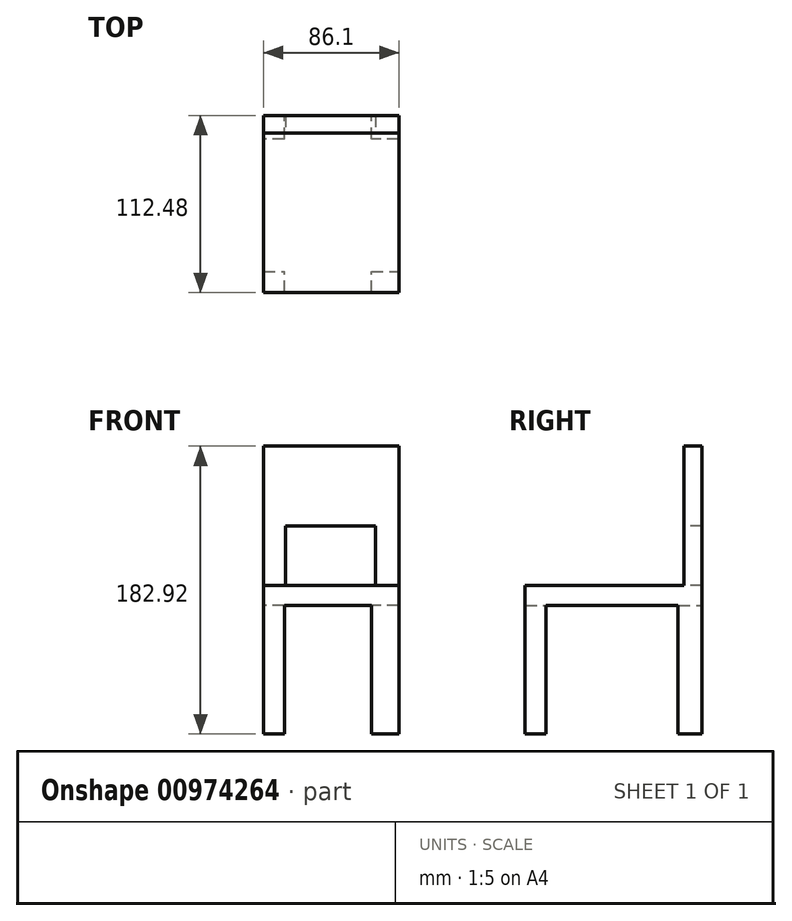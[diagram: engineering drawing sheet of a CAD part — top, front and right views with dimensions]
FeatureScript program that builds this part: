
annotation { "Feature Type Name" : "Feature", "Feature Type Description" : "" }
export const myFeature = defineFeature(function(context is Context, id is Id, definition is map)
    precondition{}
    {
        {
            var Q0;
            Q0=qCreatedBy(makeId("Top.planeOp"),FACE);
            var sketch = newSketch(context, id + "F0", { "sketchPlane" : qUnion([Q0])});
            skLineSegment(sketch, "E0.bottom", {"start": v(-38.64, 51.36) * mm, "end": v(47.46, 51.36) * mm});
            skLineSegment(sketch, "E0.top", {"start": v(-38.64, -61.12) * mm, "end": v(47.46, -61.12) * mm});
            skLineSegment(sketch, "E0.left", {"start": v(-38.64, 51.36) * mm, "end": v(-38.64, -61.12) * mm});
            skLineSegment(sketch, "E0.right", {"start": v(47.46, 51.36) * mm, "end": v(47.46, -61.12) * mm});
            skSolve(sketch);
        }
        {
            var Q0;
            Q0=makeQuery(id+"F0.imprint","IMPRINT",FACE,{"disambiguationData":[TD([[makeQuery(id+"F0.imprint","IMPRINT",EDGE,{"derivedFrom":sQuery(id+"F0.wireOp",EDGE,"E0.bottom")}),-1.0]])]});
            extrude(context, id + "F1", {"entities" : qUnion([Q0]), "depth" : 12.7 * mm, "offsetDistance" : 25.4 * mm});
        }
        {
            var Q0;
            Q0=makeQuery(id+"F1.opExtrude","CAP_FACE",FACE,{"disambiguationData":[OSD([sQuery(id+"F0.wireOp",EDGE,"E0.bottom"),sQuery(id+"F0.wireOp",EDGE,"E0.top"),sQuery(id+"F0.wireOp",EDGE,"E0.left"),sQuery(id+"F0.wireOp",EDGE,"E0.right")])],"isStart":false});
            var sketch = newSketch(context, id + "F2", { "sketchPlane" : qUnion([Q0])});
            skLineSegment(sketch, "E1", {"start": v(32.6, 51.36) * mm, "end": v(32.6, -61.12) * mm});
            skLineSegment(sketch, "E2", {"start": v(-24.73, 51.36) * mm, "end": v(-24.73, -61.12) * mm});
            skLineSegment(sketch, "E3", {"start": v(47.46, 40.03) * mm, "end": v(-38.64, 40.03) * mm});
            skLineSegment(sketch, "E4", {"start": v(47.46, -45.23) * mm, "end": v(-38.64, -45.23) * mm});
            skSolve(sketch);
        }
        {
            var Q0;
            {var subQ0=sQuery(id+"F2.wireOp",EDGE,"E2");var subQ1=makeQuery(id+"F1.opExtrude","CAP_EDGE",EDGE,{"disambiguationData":[OSD([sQuery(id+"F0.wireOp",EDGE,"E0.bottom")])],"isStart":false});var subQ2=makeQuery(id+"F2.imprint","INTERSECT",VERTEX,{"derivedFrom":[subQ1,subQ0]});Q0=makeQuery(id+"F2.imprint","IMPRINT",FACE,{"disambiguationData":[TD([[makeQuery(id+"F2.imprint","IMPRINT",EDGE,{"disambiguationData":[TD([[subQ2,-1.0]])],"derivedFrom":subQ0}),-1.0]])]});}
            var Q1;
            {var subQ0=sQuery(id+"F2.wireOp",EDGE,"E1");var subQ1=makeQuery(id+"F1.opExtrude","CAP_EDGE",EDGE,{"disambiguationData":[OSD([sQuery(id+"F0.wireOp",EDGE,"E0.bottom")])],"isStart":false});var subQ2=makeQuery(id+"F2.imprint","INTERSECT",VERTEX,{"derivedFrom":[subQ1,subQ0]});Q1=makeQuery(id+"F2.imprint","IMPRINT",FACE,{"disambiguationData":[TD([[makeQuery(id+"F2.imprint","IMPRINT",EDGE,{"disambiguationData":[TD([[subQ2,-1.0]])],"derivedFrom":subQ0}),1.0]])]});}
            extrude(context, id + "F3", {"entities" : qUnion([Q0, Q1]), "operationType" : NewBodyOperationType.ADD, "depth" : 88.57 * mm, "offsetDistance" : 25.4 * mm});
        }
        {
            var Q0;
            Q0=makeQuery(id+"F1.opExtrude","CAP_FACE",FACE,{"disambiguationData":[OSD([sQuery(id+"F0.wireOp",EDGE,"E0.bottom"),sQuery(id+"F0.wireOp",EDGE,"E0.top"),sQuery(id+"F0.wireOp",EDGE,"E0.left"),sQuery(id+"F0.wireOp",EDGE,"E0.right")])],"isStart":true});
            var sketch = newSketch(context, id + "F4", { "sketchPlane" : qUnion([Q0])});
            skLineSegment(sketch, "E5", {"start": v(-38.64, 47.8) * mm, "end": v(47.46, 47.8) * mm});
            skLineSegment(sketch, "E6", {"start": v(47.46, -36.21) * mm, "end": v(-38.64, -36.21) * mm});
            skLineSegment(sketch, "E7", {"start": v(29.9, 61.12) * mm, "end": v(29.9, -51.36) * mm});
            skLineSegment(sketch, "E8", {"start": v(-25.25, 61.12) * mm, "end": v(-25.25, -51.36) * mm});
            skSolve(sketch);
        }
        {
            var Q0;
            {var subQ0=sQuery(id+"F4.wireOp",EDGE,"E5");var subQ1=makeQuery(id+"F1.opExtrude","CAP_EDGE",EDGE,{"disambiguationData":[OSD([sQuery(id+"F0.wireOp",EDGE,"E0.right")])],"isStart":true});var subQ2=makeQuery(id+"F4.imprint","INTERSECT",VERTEX,{"derivedFrom":[subQ1,subQ0]});Q0=makeQuery(id+"F4.imprint","IMPRINT",FACE,{"disambiguationData":[TD([[makeQuery(id+"F4.imprint","IMPRINT",EDGE,{"disambiguationData":[TD([[subQ2,1.0]])],"derivedFrom":subQ0}),1.0]])]});}
            var Q1;
            {var subQ0=sQuery(id+"F4.wireOp",EDGE,"E6");var subQ1=makeQuery(id+"F1.opExtrude","CAP_EDGE",EDGE,{"disambiguationData":[OSD([sQuery(id+"F0.wireOp",EDGE,"E0.right")])],"isStart":true});var subQ2=makeQuery(id+"F4.imprint","INTERSECT",VERTEX,{"derivedFrom":[subQ1,subQ0]});Q1=makeQuery(id+"F4.imprint","IMPRINT",FACE,{"disambiguationData":[TD([[makeQuery(id+"F4.imprint","IMPRINT",EDGE,{"disambiguationData":[TD([[subQ2,-1.0]])],"derivedFrom":subQ0}),1.0]])]});}
            var Q2;
            {var subQ0=sQuery(id+"F4.wireOp",EDGE,"E6");var subQ1=makeQuery(id+"F1.opExtrude","CAP_EDGE",EDGE,{"disambiguationData":[OSD([sQuery(id+"F0.wireOp",EDGE,"E0.left")])],"isStart":true});var subQ2=makeQuery(id+"F4.imprint","INTERSECT",VERTEX,{"derivedFrom":[subQ1,subQ0]});Q2=makeQuery(id+"F4.imprint","IMPRINT",FACE,{"disambiguationData":[TD([[makeQuery(id+"F4.imprint","IMPRINT",EDGE,{"disambiguationData":[TD([[subQ2,1.0]])],"derivedFrom":subQ0}),1.0]])]});}
            var Q3;
            {var subQ0=sQuery(id+"F4.wireOp",EDGE,"E5");var subQ1=makeQuery(id+"F1.opExtrude","CAP_EDGE",EDGE,{"disambiguationData":[OSD([sQuery(id+"F0.wireOp",EDGE,"E0.left")])],"isStart":true});var subQ2=makeQuery(id+"F4.imprint","INTERSECT",VERTEX,{"derivedFrom":[subQ1,subQ0]});Q3=makeQuery(id+"F4.imprint","IMPRINT",FACE,{"disambiguationData":[TD([[makeQuery(id+"F4.imprint","IMPRINT",EDGE,{"disambiguationData":[TD([[subQ2,-1.0]])],"derivedFrom":subQ0}),1.0]])]});}
            extrude(context, id + "F5", {"entities" : qUnion([Q0, Q1, Q2, Q3]), "operationType" : NewBodyOperationType.ADD, "depth" : 71.5 * mm, "offsetDistance" : 25.4 * mm});
        }
        {
            var Q0;
            Q0=makeQuery(id+"F3.opExtrude","SWEPT_FACE",FACE,{"disambiguationData":[OSD([sQuery(id+"F2.wireOp",EDGE,"E2")])]});
            var sketch = newSketch(context, id + "F6", { "sketchPlane" : qUnion([Q0])});
            skLineSegment(sketch, "E9", {"start": v(51.36, 50.62) * mm, "end": v(40.03, 50.62) * mm});
            skPoint(sketch, "E9.endSnap0", {"position": v(40.03, 56.98) * mm});
            skSolve(sketch);
        }
        {
            var Q0;
            {var subQ0=sQuery(id+"F6.wireOp",EDGE,"E9");Q0=makeQuery(id+"F6.imprint","IMPRINT",FACE,{"disambiguationData":[TD([[makeQuery(id+"F6.imprint","IMPRINT",EDGE,{"derivedFrom":subQ0}),-1.0]])]});}
            var Q1;
            Q1=makeQuery(id+"F3.opExtrude","SWEPT_FACE",FACE,{"disambiguationData":[OSD([sQuery(id+"F2.wireOp",EDGE,"E1")])]});
            extrude(context, id + "F7", {"entities" : qUnion([Q0]), "operationType" : NewBodyOperationType.ADD, "endBound" : BoundingType.UP_TO_SURFACE, "depth" : 25.4 * mm, "endBoundEntityFace" : qUnion([Q1]), "offsetDistance" : 25.4 * mm});
        }
        {
            var Q0;
            Q0=makeQuery(id+"F5.opExtrude","CAP_FACE",FACE,{"disambiguationData":[OSD([sQuery(id+"F0.wireOp",EDGE,"E0.bottom"),sQuery(id+"F0.wireOp",EDGE,"E0.left"),sQuery(id+"F4.wireOp",EDGE,"E6"),sQuery(id+"F4.wireOp",EDGE,"E8")])],"isStart":false});
            var Q1;
            Q1=makeQuery(id+"F5.opExtrude","CAP_FACE",FACE,{"disambiguationData":[OSD([sQuery(id+"F0.wireOp",EDGE,"E0.bottom"),sQuery(id+"F0.wireOp",EDGE,"E0.right"),sQuery(id+"F4.wireOp",EDGE,"E6"),sQuery(id+"F4.wireOp",EDGE,"E7")])],"isStart":false});
            var Q2;
            Q2=makeQuery(id+"F5.opExtrude","CAP_FACE",FACE,{"disambiguationData":[OSD([sQuery(id+"F0.wireOp",EDGE,"E0.top"),sQuery(id+"F0.wireOp",EDGE,"E0.left"),sQuery(id+"F4.wireOp",EDGE,"E5"),sQuery(id+"F4.wireOp",EDGE,"E8")])],"isStart":false});
            var Q3;
            Q3=makeQuery(id+"F5.opExtrude","CAP_FACE",FACE,{"disambiguationData":[OSD([sQuery(id+"F0.wireOp",EDGE,"E0.top"),sQuery(id+"F0.wireOp",EDGE,"E0.right"),sQuery(id+"F4.wireOp",EDGE,"E5"),sQuery(id+"F4.wireOp",EDGE,"E7")])],"isStart":false});
            extrude(context, id + "F8", {"entities" : qUnion([Q0, Q1, Q2, Q3]), "operationType" : NewBodyOperationType.ADD, "depth" : 10.16 * mm, "offsetDistance" : 25.4 * mm});
        }
    });
